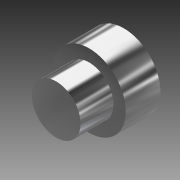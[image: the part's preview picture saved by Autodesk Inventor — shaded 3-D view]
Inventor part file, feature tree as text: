
AUTODESK INVENTOR PART (.ipt)
format: ipt  version: 2014 (Build 180170000, 170)  size: 89,600 bytes
history: native  units: in
note: dims shown in document units (in); Inventor stores cm internally (conversion verified against a paired STEP export)
features: extrude x2, sketch x2
ambient origin geometry x8: Origin, YZ Plane, XZ Plane, XY Plane, X Axis, Y Axis, Z Axis, Center Point
bodies: Solid1 (feature_tree)
feature tree (4):
  extrude  "Extrusion1"  Depth=0.2803in TaperAngle=0.0deg
  extrude  "Extrusion2"  Depth=0.2657in TaperAngle=0.0deg
  sketch  "Sketch1"  dims[d0=0.5906in d1=0.2803in d2=0.0in]
  sketch  "Sketch2"  dims[d3=0.3937in d4=0.2657in d5=0.0in]
